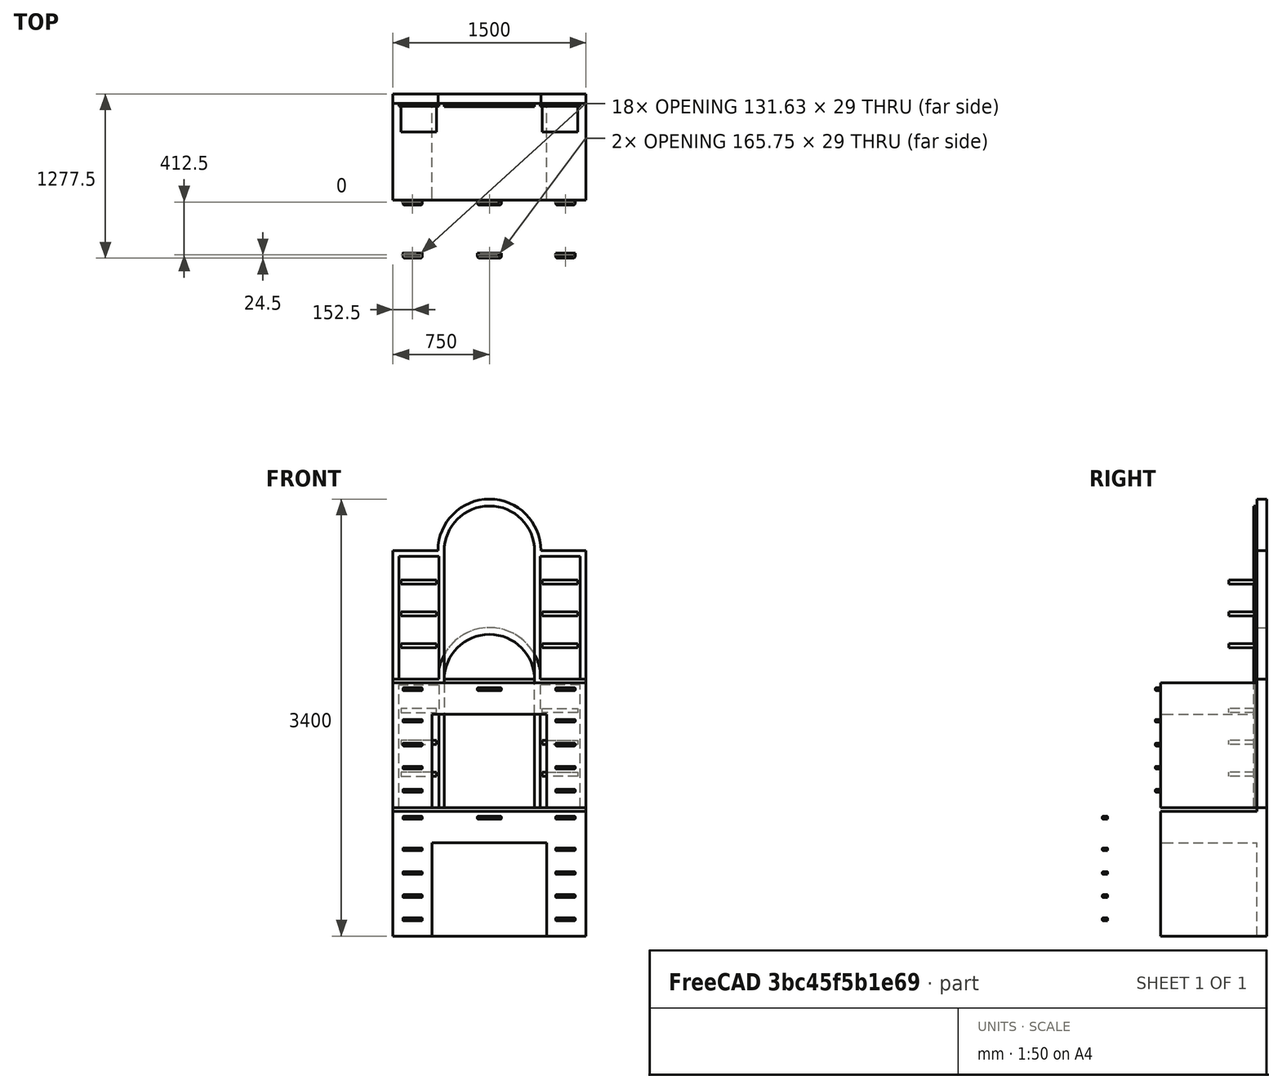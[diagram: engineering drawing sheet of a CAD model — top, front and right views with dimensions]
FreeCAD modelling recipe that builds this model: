
FCSTD DOCUMENT  (FreeCAD 1.0R39109 (Git))
Label: Dressing_Table
License: All rights reserved
LicenseURL: https://en.wikipedia.org/wiki/All_rights_reserved
objects: Sketcher::SketchObject×30, PartDesign::Fillet×22, PartDesign::Pad×18, PartDesign::Body×13, PartDesign::Pocket×12, PartDesign::ShapeBinder×12, PartDesign::Plane×12, Assembly::JointGroup×3, App::Link×3, Assembly::AssemblyObject×3, Part::FeaturePython×3, App::Part×2
note: 256 computed .brp shape members not serialized (recipe doc carries the construction recipe); baked Part::Feature solids carry a one-line shape summary decoded from their .brp

FEATURE [Sketcher::SketchObject] Sketch
  ArcFitTolerance = 1e-06
  AttachmentSupport = -> [XZ_Plane]
  FullyConstrained = true
  MakeInternals = false
  MapMode = 5
  Placement = pos=(0,0,0) rot=(1,0,0;1.5708rad)
  sketch-geometry (7):
    g0: LineSegment StartX=-750 StartY=-1000 StartZ=0 EndX=750 EndY=-1000 EndZ=0
    g1: LineSegment StartX=750 StartY=-1000 StartZ=0 EndX=750 EndY=1000 EndZ=0
    g2: LineSegment StartX=750 StartY=1000 StartZ=0 EndX=400 EndY=1000 EndZ=0
    g3: LineSegment StartX=-750 StartY=1000 StartZ=0 EndX=-750 EndY=-1000 EndZ=0
    g4: GeomPoint [constr] X=0 Y=0 Z=0
    g5: ArcOfCircle CenterX=1.35e-14 CenterY=1000 CenterZ=0 NormalX=0 NormalY=0 NormalZ=1 AngleXU=0 Radius=400 StartAngle=0 EndAngle=3.14159
    g6: LineSegment StartX=-400 StartY=1000 StartZ=0 EndX=-750 EndY=1000 EndZ=0
  constraints (18):
    c: Coincident(g0,g1)
    c: Coincident(g1,g2)
    c: Coincident(g6,g3)
    c: Coincident(g3,g0)
    c: Horizontal(g0)
    c: Horizontal(g2)
    c: Vertical(g1)
    c: Vertical(g3)
    c: Symmetric(g2,g0,g4)
    c: Coincident(g4,g-1)
    c: DistanceY(g1,g1) = 2000
    c: DistanceX(g6,g2) = 1500
    c: Symmetric(g1,g6,g5)
    c: Diameter(g5) = 800
    c: Coincident(g5,g6)
    c: Coincident(g5,g2)
    c: Horizontal(g6)
    c: Horizontal(g5,g2)
FEATURE [PartDesign::Pad] Pad
  Direction = (0,-1,2e-16)
  Length = 75
  Length2 = 10
  Placement = pos=(0,0,0) rot=(1,0,0;1.5708rad)
  Profile = -> Sketch
  ReferenceAxis = -> Sketch [N_Axis]
  Refine = true
  Suppressed = false
  Type = 0
FEATURE [Sketcher::SketchObject] Sketch001
  ArcFitTolerance = 1e-06
  AttachmentSupport = -> [Pad]
  FullyConstrained = false
  MakeInternals = false
  MapMode = 5
  Placement = pos=(0,-75,0) rot=(1,0,0;1.5708rad)
  sketch-geometry (14):
    g0: LineSegment [constr] StartX=0 StartY=0 StartZ=0 EndX=936.468 EndY=0 EndZ=0
    g1: LineSegment [constr] StartX=0 StartY=0 StartZ=0 EndX=-879.559 EndY=0 EndZ=0
    g2: ArcOfCircle CenterX=0 CenterY=995.137 CenterZ=0 NormalX=0 NormalY=0 NormalZ=1 AngleXU=0 Radius=351.618 StartAngle=0 EndAngle=3.14159
    g3: LineSegment StartX=-351.618 StartY=995.137 StartZ=0 EndX=-351.618 EndY=0 EndZ=0
    g4: LineSegment StartX=351.618 StartY=995.137 StartZ=0 EndX=351.618 EndY=0 EndZ=0
    g5: LineSegment StartX=-351.618 StartY=0 StartZ=0 EndX=351.618 EndY=0 EndZ=0
    g6: LineSegment StartX=393.332 StartY=955.725 StartZ=0 EndX=393.332 EndY=0 EndZ=0
    g7: LineSegment StartX=393.332 StartY=0 StartZ=0 EndX=704.851 EndY=0 EndZ=0
    g8: LineSegment StartX=704.851 StartY=0 StartZ=0 EndX=704.851 EndY=955.725 EndZ=0
    g9: LineSegment StartX=704.851 StartY=955.725 StartZ=0 EndX=393.332 EndY=955.725 EndZ=0
    g10: LineSegment StartX=-393.332 StartY=955.725 StartZ=0 EndX=-393.332 EndY=0 EndZ=0
    g11: LineSegment StartX=-393.332 StartY=0 StartZ=0 EndX=-704.851 EndY=0 EndZ=0
    g12: LineSegment StartX=-704.851 StartY=0 StartZ=0 EndX=-704.851 EndY=955.725 EndZ=0
    g13: LineSegment StartX=-704.851 StartY=955.725 StartZ=0 EndX=-393.332 EndY=955.725 EndZ=0
  constraints (30):
    c: Coincident(g0,g-1)
    c: Horizontal(g0)
    c: Coincident(g1,g0)
    c: PointOnObject(g1,g-1)
    c: PointOnObject(g2,g-2)
    c: PointOnObject(g3,g1)
    c: Vertical(g3)
    c: PointOnObject(g4,g0)
    c: Vertical(g4)
    c: Tangent(g4,g2) = 1.5708
    c: Tangent(g3,g2) = -1.5708
    c: Coincident(g5,g3)
    c: Coincident(g5,g4)
    c: Coincident(g6,g7)
    c: Coincident(g7,g8)
    c: Coincident(g8,g9)
    c: Coincident(g9,g6)
    c: Vertical(g6)
    c: Vertical(g8)
    c: Horizontal(g7)
    c: Horizontal(g9)
    c: PointOnObject(g7,g0)
    c: Coincident(g10,g11)
    c: Coincident(g11,g12)
    c: Coincident(g12,g13)
    c: Coincident(g13,g10)
    c: Vertical(g10)
    c: Vertical(g12)
    c: Horizontal(g11)
    c: Horizontal(g13)
FEATURE [PartDesign::Pad] Pad001
  BaseFeature = -> Pad
  Direction = (0,-1,2e-16)
  Length = 20
  Length2 = 10
  Placement = pos=(0,0,0) rot=(1,0,0;1.5708rad)
  Profile = -> Sketch001
  ReferenceAxis = -> Sketch001 [N_Axis]
  Refine = true
  Suppressed = false
  Type = 0
FEATURE [Sketcher::SketchObject] Sketch002
  ArcFitTolerance = 1e-06
  AttachmentSupport = -> [Pad001]
  ExternalGeometry = -> [Pad001]
  FullyConstrained = false
  MakeInternals = false
  MapMode = 5
  Placement = pos=(0,-95,2.09e-14) rot=(1,0,0;1.5708rad)
  sketch-geometry (27):
    g0: LineSegment StartX=-686.592 StartY=770.22 StartZ=0 EndX=-686.592 EndY=738.354 EndZ=0
    g1: LineSegment StartX=-686.592 StartY=738.354 StartZ=0 EndX=-411.592 EndY=738.354 EndZ=0
    g2: LineSegment StartX=-411.592 StartY=738.354 StartZ=0 EndX=-411.592 EndY=770.22 EndZ=0
    g3: LineSegment StartX=-411.592 StartY=770.22 StartZ=0 EndX=-686.592 EndY=770.22 EndZ=0
    g4: LineSegment StartX=-686.592 StartY=523.301 StartZ=0 EndX=-686.592 EndY=491.435 EndZ=0
    g5: LineSegment StartX=-686.592 StartY=491.435 StartZ=0 EndX=-411.592 EndY=491.435 EndZ=0
    g6: LineSegment StartX=-411.592 StartY=491.435 StartZ=0 EndX=-411.592 EndY=523.301 EndZ=0
    g7: LineSegment StartX=-411.592 StartY=523.301 StartZ=0 EndX=-686.592 EndY=523.301 EndZ=0
    g8: LineSegment StartX=-686.592 StartY=276.382 StartZ=0 EndX=-686.592 EndY=244.516 EndZ=0
    g9: LineSegment StartX=-686.592 StartY=244.516 StartZ=0 EndX=-411.592 EndY=244.516 EndZ=0
    g10: LineSegment StartX=-411.592 StartY=244.516 StartZ=0 EndX=-411.592 EndY=276.382 EndZ=0
    g11: LineSegment StartX=-411.592 StartY=276.382 StartZ=0 EndX=-686.592 EndY=276.382 EndZ=0
    g12: LineSegment [constr] StartX=-686.592 StartY=738.354 StartZ=0 EndX=-686.592 EndY=523.301 EndZ=0
    g13: LineSegment [constr] StartX=-686.592 StartY=491.435 StartZ=0 EndX=-686.592 EndY=276.382 EndZ=0
    g14: LineSegment [constr] StartX=-549.092 StartY=477.863 StartZ=0 EndX=-549.092 EndY=955.725 EndZ=0
    g15: LineSegment StartX=686.592 StartY=738.354 StartZ=0 EndX=411.592 EndY=738.354 EndZ=0
    g16: LineSegment StartX=411.592 StartY=770.22 StartZ=0 EndX=686.592 EndY=770.22 EndZ=0
    g17: LineSegment StartX=411.592 StartY=738.354 StartZ=0 EndX=411.592 EndY=770.22 EndZ=0
    g18: LineSegment StartX=686.592 StartY=770.22 StartZ=0 EndX=686.592 EndY=738.354 EndZ=0
    g19: LineSegment StartX=411.592 StartY=523.301 StartZ=0 EndX=686.592 EndY=523.301 EndZ=0
    g20: LineSegment StartX=411.592 StartY=491.435 StartZ=0 EndX=411.592 EndY=523.301 EndZ=0
    g21: LineSegment StartX=686.592 StartY=491.435 StartZ=0 EndX=411.592 EndY=491.435 EndZ=0
    g22: LineSegment StartX=686.592 StartY=523.301 StartZ=0 EndX=686.592 EndY=491.435 EndZ=0
    g23: LineSegment StartX=411.592 StartY=244.516 StartZ=0 EndX=411.592 EndY=276.382 EndZ=0
    g24: LineSegment StartX=686.592 StartY=244.516 StartZ=0 EndX=411.592 EndY=244.516 EndZ=0
    g25: LineSegment StartX=411.592 StartY=276.382 StartZ=0 EndX=686.592 EndY=276.382 EndZ=0
    g26: LineSegment StartX=686.592 StartY=276.382 StartZ=0 EndX=686.592 EndY=244.516 EndZ=0
  constraints (66):
    c: Coincident(g0,g1)
    c: Coincident(g1,g2)
    c: Coincident(g2,g3)
    c: Coincident(g3,g0)
    c: Vertical(g0)
    c: Vertical(g2)
    c: Horizontal(g1)
    c: Horizontal(g3)
    c: Coincident(g4,g5)
    c: Coincident(g5,g6)
    c: Coincident(g6,g7)
    c: Coincident(g7,g4)
    c: Vertical(g4)
    c: Vertical(g6)
    c: Horizontal(g5)
    c: Horizontal(g7)
    c: Coincident(g8,g9)
    c: Coincident(g9,g10)
    c: Coincident(g10,g11)
    c: Coincident(g11,g8)
    c: Vertical(g8)
    c: Vertical(g10)
    c: Horizontal(g9)
    c: Horizontal(g11)
    c: Coincident(g12,g0)
    c: Coincident(g12,g4)
    c: Vertical(g12)
    c: Coincident(g13,g4)
    c: Coincident(g13,g8)
    c: Vertical(g13)
    c: Equal(g12,g13)
    c: Equal(g2,g6)
    c: Equal(g6,g10)
    c: Equal(g11,g7)
    c: Equal(g7,g3)
    c: DistanceX(g3,g3) = 275
    c: Symmetric(g2,g0,g14)
    c: Symmetric(g-5,g-5,g14)
    c: Coincident(g18,g15)
    c: Coincident(g15,g17)
    c: Coincident(g17,g16)
    c: Coincident(g16,g18)
    c: Vertical(g18)
    c: Vertical(g17)
    c: Horizontal(g15)
    c: Horizontal(g16)
    c: Coincident(g22,g21)
    c: Coincident(g21,g20)
    c: Coincident(g20,g19)
    c: Coincident(g19,g22)
    c: Vertical(g22)
    c: Vertical(g20)
    c: Horizontal(g21)
    c: Horizontal(g19)
    c: Coincident(g26,g24)
    c: Coincident(g24,g23)
    c: Coincident(g23,g25)
    c: Coincident(g25,g26)
    c: Vertical(g26)
    c: Vertical(g23)
    c: Horizontal(g24)
    c: Horizontal(g25)
    c: Equal(g17,g20)
    c: Equal(g20,g23)
    c: Equal(g25,g19)
    c: Equal(g19,g16)
FEATURE [PartDesign::Pad] Pad002
  BaseFeature = -> Pad001
  Direction = (0,-1,2e-16)
  Length = 200
  Length2 = 10
  Placement = pos=(0,0,0) rot=(1,0,0;1.5708rad)
  Profile = -> Sketch002
  ReferenceAxis = -> Sketch002 [N_Axis]
  Refine = true
  Suppressed = false
  Type = 0
FEATURE [Sketcher::SketchObject] Sketch003
  ArcFitTolerance = 1e-06
  AttachmentSupport = -> [Pad002]
  ExternalGeometry = -> [Pad002]
  FullyConstrained = true
  MakeInternals = false
  MapMode = 5
  Placement = pos=(0,-75,0) rot=(1,0,0;1.5708rad)
  sketch-geometry (4):
    g0: LineSegment StartX=-750 StartY=-1000 StartZ=0 EndX=750 EndY=-1000 EndZ=0
    g1: LineSegment StartX=750 StartY=-1000 StartZ=0 EndX=750 EndY=-30 EndZ=0
    g2: LineSegment StartX=750 StartY=-30 StartZ=0 EndX=-750 EndY=-30 EndZ=0
    g3: LineSegment StartX=-750 StartY=-30 StartZ=0 EndX=-750 EndY=-1000 EndZ=0
  constraints (11):
    c: Coincident(g0,g1)
    c: Coincident(g1,g2)
    c: Coincident(g2,g3)
    c: Coincident(g3,g0)
    c: Horizontal(g0)
    c: Horizontal(g2)
    c: Vertical(g1)
    c: Vertical(g3)
    c: Coincident(g0,g-3)
    c: PointOnObject(g1,g-4)
    c: DistanceY(g1,g1) = 970
FEATURE [PartDesign::Pad] Pad003
  BaseFeature = -> Pad002
  Direction = (0,-1,2e-16)
  Length = 750
  Length2 = 10
  Placement = pos=(0,0,0) rot=(1,0,0;1.5708rad)
  Profile = -> Sketch003
  ReferenceAxis = -> Sketch003 [N_Axis]
  Suppressed = false
  Type = 0
FEATURE [Sketcher::SketchObject] Sketch004
  ArcFitTolerance = 1e-06
  AttachmentSupport = -> [Pad003]
  ExternalGeometry = -> [Pad003]
  FullyConstrained = true
  MakeInternals = false
  MapMode = 5
  Placement = pos=(0,-825,1.897e-13) rot=(1,0,0;1.5708rad)
  sketch-geometry (4):
    g0: LineSegment StartX=-445 StartY=-1000 StartZ=0 EndX=445 EndY=-1000 EndZ=0
    g1: LineSegment StartX=445 StartY=-1000 StartZ=0 EndX=445 EndY=-275 EndZ=0
    g2: LineSegment StartX=445 StartY=-275 StartZ=0 EndX=-445 EndY=-275 EndZ=0
    g3: LineSegment StartX=-445 StartY=-275 StartZ=0 EndX=-445 EndY=-1000 EndZ=0
  constraints (11):
    c: Coincident(g0,g1)
    c: Coincident(g1,g2)
    c: Coincident(g2,g3)
    c: Coincident(g3,g0)
    c: Horizontal(g0)
    c: Vertical(g1)
    c: Vertical(g3)
    c: PointOnObject(g0,g-3)
    c: DistanceX(g2,g2) = 890
    c: DistanceY(g1,g1) = 725
    c: Symmetric(g1,g2,g-2)
FEATURE [PartDesign::Pocket] Pocket
  BaseFeature = -> Pad003
  Direction = (0,1,-2e-16)
  Length = 750
  Length2 = 5
  Placement = pos=(0,0,0) rot=(1,0,0;1.5708rad)
  Profile = -> Sketch004
  ReferenceAxis = -> Sketch004 [N_Axis]
  Suppressed = false
  Type = 0
FEATURE [Sketcher::SketchObject] Sketch005
  ArcFitTolerance = 1e-06
  AttachmentSupport = -> [Pocket]
  ExternalGeometry = -> [Pocket]
  FullyConstrained = true
  MakeInternals = false
  MapMode = 5
  Placement = pos=(0,-825,1.897e-13) rot=(1,0,0;1.5708rad)
  sketch-geometry (24):
    g0: LineSegment StartX=-445 StartY=-275 StartZ=0 EndX=-445 EndY=-30 EndZ=0
    g1: LineSegment StartX=-445 StartY=-30 StartZ=0 EndX=-750 EndY=-30 EndZ=0
    g2: LineSegment StartX=-750 StartY=-30 StartZ=0 EndX=-750 EndY=-275 EndZ=0
    g3: LineSegment StartX=-750 StartY=-275 StartZ=0 EndX=-445 EndY=-275 EndZ=0
    g4: LineSegment StartX=-445 StartY=-460 StartZ=0 EndX=-750 EndY=-460 EndZ=0
    g5: LineSegment StartX=-750 StartY=-460 StartZ=0 EndX=-750 EndY=-640 EndZ=0
    g6: LineSegment StartX=-750 StartY=-640 StartZ=0 EndX=-445 EndY=-640 EndZ=0
    g7: LineSegment StartX=-445 StartY=-640 StartZ=0 EndX=-445 EndY=-460 EndZ=0
    g8: LineSegment StartX=-750 StartY=-820 StartZ=0 EndX=-445 EndY=-820 EndZ=0
    g9: LineSegment StartX=-750 StartY=-820 StartZ=0 EndX=-750 EndY=-1000 EndZ=0
    g10: LineSegment StartX=-750 StartY=-1000 StartZ=0 EndX=-445 EndY=-1000 EndZ=0
    g11: LineSegment StartX=-445 StartY=-1000 StartZ=0 EndX=-445 EndY=-820 EndZ=0
    g12: LineSegment StartX=750 StartY=-30 StartZ=0 EndX=750 EndY=-275 EndZ=0
    g13: LineSegment StartX=445 StartY=-30 StartZ=0 EndX=750 EndY=-30 EndZ=0
    g14: LineSegment StartX=750 StartY=-275 StartZ=0 EndX=445 EndY=-275 EndZ=0
    g15: LineSegment StartX=445 StartY=-460 StartZ=0 EndX=750 EndY=-460 EndZ=0
    g16: LineSegment StartX=750 StartY=-460 StartZ=0 EndX=750 EndY=-640 EndZ=0
    g17: LineSegment StartX=750 StartY=-640 StartZ=0 EndX=445 EndY=-640 EndZ=0
    g18: LineSegment StartX=445 StartY=-640 StartZ=0 EndX=445 EndY=-460 EndZ=0
    g19: LineSegment StartX=445 StartY=-1000 StartZ=0 EndX=445 EndY=-820 EndZ=0
    g20: LineSegment StartX=750 StartY=-1000 StartZ=0 EndX=445 EndY=-1000 EndZ=0
    g21: LineSegment StartX=750 StartY=-820 StartZ=0 EndX=750 EndY=-1000 EndZ=0
    g22: LineSegment StartX=750 StartY=-820 StartZ=0 EndX=445 EndY=-820 EndZ=0
    g23: LineSegment StartX=445 StartY=-30 StartZ=0 EndX=445 EndY=-275 EndZ=0
  constraints (67):
    c: Coincident(g0,g1)
    c: Vertical(g0)
    c: Horizontal(g1)
    c: Coincident(g0,g-6)
    c: Coincident(g1,g2)
    c: PointOnObject(g2,g-5)
    c: Coincident(g2,g3)
    c: Coincident(g3,g0)
    c: Horizontal(g3)
    c: PointOnObject(g4,g-6)
    c: PointOnObject(g4,g-5)
    c: Horizontal(g4)
    c: Coincident(g4,g5)
    c: PointOnObject(g5,g-5)
    c: Coincident(g5,g6)
    c: PointOnObject(g6,g-6)
    c: Horizontal(g6)
    c: Coincident(g6,g7)
    c: PointOnObject(g8,g-5)
    c: PointOnObject(g8,g-6)
    c: Horizontal(g8)
    c: Coincident(g9,g10)
    c: PointOnObject(g10,g-6)
    c: Horizontal(g10)
    c: Coincident(g10,g11)
    c: Coincident(g11,g8)
    c: Coincident(g9,g-5)
    c: DistanceY(g9,g9) = 180
    c: Coincident(g1,g-5)
    c: Horizontal(g13)
    c: Coincident(g13,g12)
    c: Coincident(g12,g14)
    c: Horizontal(g14)
    c: Horizontal(g15)
    c: Coincident(g15,g16)
    c: Coincident(g16,g17)
    c: Horizontal(g17)
    c: Coincident(g17,g18)
    c: Horizontal(g22)
    c: Coincident(g21,g20)
    c: Horizontal(g20)
    c: Coincident(g20,g19)
    c: Coincident(g19,g22)
    c: Coincident(g12,g-4)
    c: Equal(g14,g13)
    c: Horizontal(g15,g4)
    c: Horizontal(g17,g6)
    c: Horizontal(g22,g8)
    c: Horizontal(g19,g10)
    c: Vertical(g15,g17)
    c: Vertical(g17,g22)
    c: Vertical(g22,g19)
    c: Vertical(g19,g14)
    c: Vertical(g21,g20)
    c: Vertical(g20,g12)
    c: Coincident(g23,g13)
    c: Coincident(g23,g14)
    c: Vertical(g23)
    c: Coincident(g14,g-3)
    c: Coincident(g7,g4)
    c: Equal(g5,g9)
    c: Coincident(g18,g15)
    c: Vertical(g15,g12)
    c: Coincident(g22,g21)
    c: Coincident(g9,g8)
    c: DistanceY(g8,g5) = 180
    c: Vertical(g16,g21)
FEATURE [PartDesign::Pad] Pad004
  BaseFeature = -> Pocket
  Direction = (0,-1,2e-16)
  Length = 25
  Length2 = 10
  Placement = pos=(0,0,0) rot=(1,0,0;1.5708rad)
  Profile = -> Sketch005
  ReferenceAxis = -> Sketch005 [N_Axis]
  Reversed = true
  Suppressed = false
  Type = 0
FEATURE [Sketcher::SketchObject] Sketch006
  ArcFitTolerance = 1e-06
  AttachmentSupport = -> [Pad004]
  ExternalGeometry = -> [Pad004]
  FullyConstrained = true
  MakeInternals = false
  MapMode = 5
  Placement = pos=(0,-825,1.897e-13) rot=(1,0,0;1.5708rad)
  sketch-geometry (20):
    g0: LineSegment StartX=-750 StartY=-275 StartZ=0 EndX=-750 EndY=-460 EndZ=0
    g1: LineSegment StartX=-750 StartY=-460 StartZ=0 EndX=-445 EndY=-460 EndZ=0
    g2: LineSegment StartX=-445 StartY=-460 StartZ=0 EndX=-445 EndY=-275 EndZ=0
    g3: LineSegment StartX=-445 StartY=-275 StartZ=0 EndX=-750 EndY=-275 EndZ=0
    g4: LineSegment StartX=-750 StartY=-640 StartZ=0 EndX=-750 EndY=-820 EndZ=0
    g5: LineSegment StartX=-750 StartY=-820 StartZ=0 EndX=-445 EndY=-820 EndZ=0
    g6: LineSegment StartX=-445 StartY=-820 StartZ=0 EndX=-445 EndY=-640 EndZ=0
    g7: LineSegment StartX=-445 StartY=-640 StartZ=0 EndX=-750 EndY=-640 EndZ=0
    g8: LineSegment StartX=445 StartY=-275 StartZ=0 EndX=445 EndY=-460 EndZ=0
    g9: LineSegment StartX=445 StartY=-460 StartZ=0 EndX=750 EndY=-460 EndZ=0
    g10: LineSegment StartX=750 StartY=-460 StartZ=0 EndX=750 EndY=-275 EndZ=0
    g11: LineSegment StartX=750 StartY=-275 StartZ=0 EndX=445 EndY=-275 EndZ=0
    g12: LineSegment StartX=445 StartY=-640 StartZ=0 EndX=445 EndY=-820 EndZ=0
    g13: LineSegment StartX=445 StartY=-820 StartZ=0 EndX=750 EndY=-820 EndZ=0
    g14: LineSegment StartX=750 StartY=-820 StartZ=0 EndX=750 EndY=-640 EndZ=0
    g15: LineSegment StartX=750 StartY=-640 StartZ=0 EndX=445 EndY=-640 EndZ=0
    g16: LineSegment StartX=-445 StartY=-30 StartZ=0 EndX=-445 EndY=-275 EndZ=0
    g17: LineSegment StartX=-445 StartY=-275 StartZ=0 EndX=445 EndY=-275 EndZ=0
    g18: LineSegment StartX=445 StartY=-275 StartZ=0 EndX=445 EndY=-30 EndZ=0
    g19: LineSegment StartX=445 StartY=-30 StartZ=0 EndX=-445 EndY=-30 EndZ=0
  constraints (50):
    c: Coincident(g0,g1)
    c: Coincident(g1,g2)
    c: Coincident(g2,g3)
    c: Coincident(g3,g0)
    c: Vertical(g0)
    c: Vertical(g2)
    c: Horizontal(g1)
    c: Horizontal(g3)
    c: Coincident(g0,g-4)
    c: Coincident(g1,g-3)
    c: Coincident(g4,g5)
    c: Coincident(g5,g6)
    c: Coincident(g6,g7)
    c: Coincident(g7,g4)
    c: Vertical(g4)
    c: Vertical(g6)
    c: Horizontal(g5)
    c: Horizontal(g7)
    c: Coincident(g4,g-6)
    c: Coincident(g5,g-5)
    c: Coincident(g8,g9)
    c: Coincident(g9,g10)
    c: Coincident(g10,g11)
    c: Coincident(g11,g8)
    c: Vertical(g8)
    c: Vertical(g10)
    c: Horizontal(g9)
    c: Horizontal(g11)
    c: Coincident(g8,g-8)
    c: Coincident(g9,g-9)
    c: Coincident(g12,g13)
    c: Coincident(g13,g14)
    c: Coincident(g14,g15)
    c: Coincident(g15,g12)
    c: Vertical(g12)
    c: Vertical(g14)
    c: Horizontal(g13)
    c: Horizontal(g15)
    c: Coincident(g12,g-10)
    c: Coincident(g13,g-11)
    c: Coincident(g16,g17)
    c: Coincident(g17,g18)
    c: Coincident(g18,g19)
    c: Coincident(g19,g16)
    c: Vertical(g16)
    c: Vertical(g18)
    c: Horizontal(g17)
    c: Horizontal(g19)
    c: Coincident(g16,g-7)
    c: Coincident(g17,g8)
FEATURE [PartDesign::Pad] Pad005
  BaseFeature = -> Pad004
  Direction = (0,-1,2e-16)
  Length = 25
  Length2 = 10
  Placement = pos=(0,0,0) rot=(1,0,0;1.5708rad)
  Profile = -> Sketch006
  ReferenceAxis = -> Sketch006 [N_Axis]
  Reversed = true
  Suppressed = false
  Type = 0
FEATURE [PartDesign::Body] Body
  AllowCompound = false
  Group = -> [Sketch,Pad,Sketch001,Pad001,Sketch002,Pad002,Sketch003,Pad003,Sketch004,Pocket,Sketch005,Pad004,Sketch006,Pad005]
  Origin = -> Origin
  Placement = pos=(0,412.5,0) rot=(0,0,1;0rad)
  Tip = -> Pad005
FEATURE [Assembly::JointGroup] Joints
FEATURE [App::Link] dressing_table001  label="dressing_table002"
  LinkPlacement = pos=(0,412.5,1000) rot=(0,0,1;0rad)
  LinkedObject = -> Body
  Placement = pos=(0,412.5,1000) rot=(0,0,1;0rad)
FEATURE [Assembly::AssemblyObject] Assembly  label="body_a"
  Group = -> [Joints,dressing_table001]
  Origin = -> Origin003
  Placement = pos=(0,412.5,1000) rot=(0,0,1;0rad)
  Type = Assembly
FEATURE [PartDesign::ShapeBinder] CopyPocket001
  Placement = pos=(0,0,0) rot=(1,0,0;1.5708rad)
  TraceSupport = false
FEATURE [PartDesign::Plane] DatumPlane
  AttachmentSupport = -> [CopyPocket001]
  Length = 214.996
  MapMode = 5
  Placement = pos=(0,-825,6.6e-15) rot=(1,0,0;1.5708rad)
  ResizeMode = 0
  Width = 144.392
FEATURE [Sketcher::SketchObject] Sketch008
  ArcFitTolerance = 1e-06
  AttachmentSupport = -> [CopyPocket001]
  ExternalGeometry = -> [CopyPocket001]
  FullyConstrained = true
  MakeInternals = false
  MapMode = 5
  Placement = pos=(0,-825,1.897e-13) rot=(1,0,0;1.5708rad)
  sketch-geometry (4):
    g0: LineSegment StartX=-92.8734 StartY=-68.8715 StartZ=0 EndX=-92.8734 EndY=-90.1429 EndZ=0
    g1: LineSegment StartX=-92.8734 StartY=-90.1429 StartZ=0 EndX=92.8734 EndY=-90.1429 EndZ=0
    g2: LineSegment StartX=92.8734 StartY=-90.1429 StartZ=0 EndX=92.8734 EndY=-68.8715 EndZ=0
    g3: LineSegment StartX=92.8734 StartY=-68.8715 StartZ=0 EndX=-92.8734 EndY=-68.8715 EndZ=0
  constraints (10):
    c: Coincident(g0,g1)
    c: Coincident(g1,g2)
    c: Coincident(g2,g3)
    c: Coincident(g3,g0)
    c: Vertical(g0)
    c: Vertical(g2)
    c: Horizontal(g1)
    c: Horizontal(g3)
    c: Coincident(g0,g-3)
    c: Coincident(g1,g-5)
FEATURE [PartDesign::Pad] Pad006
  Direction = (0,-1,2e-16)
  Length = 40
  Length2 = 10
  Placement = pos=(0,0,0) rot=(1,0,0;1.5708rad)
  Profile = -> Sketch008
  ReferenceAxis = -> Sketch008 [N_Axis]
  Refine = true
  Suppressed = false
  Type = 0
FEATURE [Sketcher::SketchObject] Sketch009
  ArcFitTolerance = 1e-06
  AttachmentSupport = -> [Pad006]
  ExternalGeometry = -> [Pad006]
  FullyConstrained = true
  MakeInternals = false
  MapMode = 5
  Placement = pos=(0,-7.6e-15,-68.8715) rot=(0,0,1;3.14159rad)
  sketch-geometry (4):
    g0: LineSegment StartX=-77.8734 StartY=850 StartZ=0 EndX=-77.8734 EndY=826 EndZ=0
    g1: LineSegment StartX=77.8734 StartY=850 StartZ=0 EndX=77.8734 EndY=826 EndZ=0
    g2: LineSegment StartX=-77.8734 StartY=850 StartZ=0 EndX=77.8734 EndY=850 EndZ=0
    g3: LineSegment StartX=-77.8734 StartY=826 StartZ=0 EndX=77.8734 EndY=826 EndZ=0
  constraints (12):
    c: Coincident(g2,g0)
    c: Coincident(g2,g1)
    c: Horizontal(g2)
    c: DistanceX(g-3,g0) = 15
    c: DistanceX(g1,g-3) = 15
    c: Vertical(g0)
    c: Vertical(g1)
    c: DistanceY(g0,g-4) = 15
    c: DistanceY(g-3,g0) = 1
    c: DistanceY(g-3,g1) = 1
    c: Coincident(g3,g0)
    c: Coincident(g3,g1)
FEATURE [PartDesign::Pocket] Pocket002
  BaseFeature = -> Pad006
  Direction = (0,0,-1)
  Length = 5
  Length2 = 5
  Placement = pos=(0,0,0) rot=(1,0,0;1.5708rad)
  Profile = -> Sketch009
  ReferenceAxis = -> Sketch009 [N_Axis]
  Refine = true
  Suppressed = false
  Type = 1
FEATURE [PartDesign::Fillet] Fillet
  Base = -> Pocket002 [Edge22,Edge21,Edge4,Edge20]
  BaseFeature = -> Pocket002
  Placement = pos=(0,0,0) rot=(1,0,0;1.5708rad)
  Radius = 15
  Refine = true
  SupportTransform = false
  Suppressed = false
  UseAllEdges = false
FEATURE [PartDesign::Fillet] Fillet001
  Base = -> Fillet [Edge8,Edge20,Edge10,Edge26]
  BaseFeature = -> Fillet
  Placement = pos=(0,0,0) rot=(1,0,0;1.5708rad)
  Radius = 5
  Refine = true
  SupportTransform = false
  Suppressed = false
  UseAllEdges = false
FEATURE [PartDesign::Body] Body001
  AllowCompound = false
  Group = -> [DatumPlane,CopyPocket001,Sketch008,Pad006,Sketch009,Pocket002,Fillet,Fillet001]
  Origin = -> Origin005
  Tip = -> Fillet001
FEATURE [PartDesign::ShapeBinder] CopyPocket002
  Placement = pos=(0,0,0) rot=(1,0,0;1.5708rad)
  TraceSupport = false
FEATURE [PartDesign::Plane] DatumPlane001
  AttachmentSupport = -> [CopyPocket002]
  Length = 755.028
  MapMode = 5
  Placement = pos=(0,-825,6.6e-15) rot=(1,0,0;1.5708rad)
  ResizeMode = 0
  Width = 171.855
FEATURE [Sketcher::SketchObject] Sketch010
  ArcFitTolerance = 1e-06
  AttachmentSupport = -> [CopyPocket002]
  ExternalGeometry = -> [CopyPocket002]
  FullyConstrained = true
  MakeInternals = false
  MapMode = 5
  Placement = pos=(0,-825,1.897e-13) rot=(1,0,0;1.5708rad)
  sketch-geometry (4):
    g0: LineSegment StartX=-673.316 StartY=-90.1429 StartZ=0 EndX=-521.684 EndY=-90.1429 EndZ=0
    g1: LineSegment StartX=-521.684 StartY=-90.1429 StartZ=0 EndX=-521.684 EndY=-68.8715 EndZ=0
    g2: LineSegment StartX=-521.684 StartY=-68.8715 StartZ=0 EndX=-673.316 EndY=-68.8715 EndZ=0
    g3: LineSegment StartX=-673.316 StartY=-68.8715 StartZ=0 EndX=-673.316 EndY=-90.1429 EndZ=0
  constraints (10):
    c: Coincident(g0,g1)
    c: Coincident(g1,g2)
    c: Coincident(g2,g3)
    c: Coincident(g3,g0)
    c: Horizontal(g0)
    c: Horizontal(g2)
    c: Vertical(g1)
    c: Vertical(g3)
    c: Coincident(g0,g-4)
    c: Coincident(g1,g-3)
FEATURE [PartDesign::Pad] Pad007
  Direction = (0,-1,2e-16)
  Length = 40
  Length2 = 10
  Placement = pos=(0,0,0) rot=(1,0,0;1.5708rad)
  Profile = -> Sketch010
  ReferenceAxis = -> Sketch010 [N_Axis]
  Refine = true
  Suppressed = false
  Type = 0
FEATURE [Sketcher::SketchObject] Sketch011
  ArcFitTolerance = 1e-06
  AttachmentSupport = -> [Pad007]
  ExternalGeometry = -> [Pad007]
  FullyConstrained = true
  MakeInternals = false
  MapMode = 5
  Placement = pos=(0,-7.6e-15,-68.8715) rot=(0,0,1;3.14159rad)
  sketch-geometry (4):
    g0: LineSegment StartX=536.684 StartY=850 StartZ=0 EndX=536.684 EndY=826 EndZ=0
    g1: LineSegment StartX=536.684 StartY=826 StartZ=0 EndX=658.316 EndY=826 EndZ=0
    g2: LineSegment StartX=658.316 StartY=826 StartZ=0 EndX=658.316 EndY=850 EndZ=0
    g3: LineSegment StartX=658.316 StartY=850 StartZ=0 EndX=536.684 EndY=850 EndZ=0
  constraints (12):
    c: Coincident(g0,g1)
    c: Coincident(g1,g2)
    c: Coincident(g2,g3)
    c: Coincident(g3,g0)
    c: Vertical(g0)
    c: Vertical(g2)
    c: Horizontal(g1)
    c: Horizontal(g3)
    c: DistanceY(g-4,g1) = 1
    c: DistanceX(g1,g-4) = 15
    c: DistanceY(g2,g-4) = 15
    c: DistanceX(g-3,g0) = 15
FEATURE [PartDesign::Pocket] Pocket003
  BaseFeature = -> Pad007
  Direction = (0,0,-1)
  Length = 5
  Length2 = 5
  Placement = pos=(0,0,0) rot=(1,0,0;1.5708rad)
  Profile = -> Sketch011
  ReferenceAxis = -> Sketch011 [N_Axis]
  Refine = true
  Suppressed = false
  Type = 1
FEATURE [PartDesign::Fillet] Fillet002
  Base = -> Pocket003 [Edge19,Edge14,Edge23,Edge11]
  BaseFeature = -> Pocket003
  Placement = pos=(0,0,0) rot=(1,0,0;1.5708rad)
  Radius = 15
  Refine = true
  SupportTransform = false
  Suppressed = false
  UseAllEdges = false
FEATURE [PartDesign::Fillet] Fillet003
  Base = -> Fillet002 [Edge21,Edge4,Edge32,Edge10]
  BaseFeature = -> Fillet002
  Placement = pos=(0,0,0) rot=(1,0,0;1.5708rad)
  Radius = 5
  Refine = true
  SupportTransform = false
  Suppressed = false
  UseAllEdges = false
FEATURE [PartDesign::Body] Body002
  AllowCompound = false
  Group = -> [DatumPlane001,CopyPocket002,Sketch010,Pad007,Sketch011,Pocket003,Fillet002,Fillet003]
  Origin = -> Origin007
  Tip = -> Fillet003
FEATURE [PartDesign::ShapeBinder] CopyPocket003
  Placement = pos=(0,0,0) rot=(1,0,0;1.5708rad)
  TraceSupport = false
FEATURE [PartDesign::Plane] DatumPlane002
  AttachmentSupport = -> [CopyPocket003]
  Length = 798.615
  MapMode = 5
  Placement = pos=(0,-825,6.6e-15) rot=(1,0,0;1.5708rad)
  ResizeMode = 0
  Width = 460.441
FEATURE [Sketcher::SketchObject] Sketch012
  ArcFitTolerance = 1e-06
  AttachmentSupport = -> [CopyPocket003]
  ExternalGeometry = -> [CopyPocket003]
  FullyConstrained = true
  MakeInternals = false
  MapMode = 5
  Placement = pos=(0,-825,1.897e-13) rot=(1,0,0;1.5708rad)
  sketch-geometry (4):
    g0: LineSegment StartX=-673.316 StartY=-313.872 StartZ=0 EndX=-673.316 EndY=-335.143 EndZ=0
    g1: LineSegment StartX=-673.316 StartY=-335.143 StartZ=0 EndX=-521.684 EndY=-335.143 EndZ=0
    g2: LineSegment StartX=-521.684 StartY=-335.143 StartZ=0 EndX=-521.684 EndY=-313.872 EndZ=0
    g3: LineSegment StartX=-521.684 StartY=-313.872 StartZ=0 EndX=-673.316 EndY=-313.872 EndZ=0
  constraints (10):
    c: Coincident(g0,g1)
    c: Coincident(g1,g2)
    c: Coincident(g2,g3)
    c: Coincident(g3,g0)
    c: Vertical(g0)
    c: Vertical(g2)
    c: Horizontal(g1)
    c: Horizontal(g3)
    c: Coincident(g0,g-4)
    c: Coincident(g1,g-3)
FEATURE [PartDesign::Pad] Pad008
  Direction = (0,-1,2e-16)
  Length = 40
  Length2 = 10
  Placement = pos=(0,0,0) rot=(1,0,0;1.5708rad)
  Profile = -> Sketch012
  ReferenceAxis = -> Sketch012 [N_Axis]
  Refine = true
  Suppressed = false
  Type = 0
FEATURE [Sketcher::SketchObject] Sketch013
  ArcFitTolerance = 1e-06
  AttachmentSupport = -> [Pad008]
  ExternalGeometry = -> [Pad008]
  FullyConstrained = true
  MakeInternals = false
  MapMode = 5
  Placement = pos=(0,-3.45e-14,-313.872) rot=(0,0,1;3.14159rad)
  sketch-geometry (4):
    g0: LineSegment StartX=536.684 StartY=850 StartZ=0 EndX=536.684 EndY=826 EndZ=0
    g1: LineSegment StartX=536.684 StartY=826 StartZ=0 EndX=658.316 EndY=826 EndZ=0
    g2: LineSegment StartX=658.316 StartY=826 StartZ=0 EndX=658.316 EndY=850 EndZ=0
    g3: LineSegment StartX=658.316 StartY=850 StartZ=0 EndX=536.684 EndY=850 EndZ=0
  constraints (12):
    c: Coincident(g0,g1)
    c: Coincident(g1,g2)
    c: Coincident(g2,g3)
    c: Coincident(g3,g0)
    c: Vertical(g0)
    c: Vertical(g2)
    c: Horizontal(g1)
    c: Horizontal(g3)
    c: DistanceY(g-4,g1) = 1
    c: DistanceX(g1,g-4) = 15
    c: DistanceY(g0,g-3) = 15
    c: DistanceX(g-3,g0) = 15
FEATURE [PartDesign::Pocket] Pocket004
  BaseFeature = -> Pad008
  Direction = (0,0,-1)
  Length = 5
  Length2 = 5
  Placement = pos=(0,0,0) rot=(1,0,0;1.5708rad)
  Profile = -> Sketch013
  ReferenceAxis = -> Sketch013 [N_Axis]
  Refine = true
  Suppressed = false
  Type = 1
FEATURE [PartDesign::Fillet] Fillet004
  Base = -> Pocket004 [Edge20,Edge4,Edge21,Edge22]
  BaseFeature = -> Pocket004
  Placement = pos=(0,0,0) rot=(1,0,0;1.5708rad)
  Radius = 15
  Refine = true
  SupportTransform = false
  Suppressed = false
  UseAllEdges = false
FEATURE [PartDesign::Fillet] Fillet005
  Base = -> Fillet004 [Edge8,Edge20,Edge10,Edge26]
  BaseFeature = -> Fillet004
  Placement = pos=(0,0,0) rot=(1,0,0;1.5708rad)
  Radius = 5
  Refine = true
  SupportTransform = false
  Suppressed = false
  UseAllEdges = false
FEATURE [PartDesign::Body] Body003
  AllowCompound = false
  Group = -> [DatumPlane002,CopyPocket003,Sketch012,Pad008,Sketch013,Pocket004,Fillet004,Fillet005]
  Origin = -> Origin008
  Tip = -> Fillet005
FEATURE [PartDesign::ShapeBinder] CopyPocket004
  Placement = pos=(0,0,0) rot=(1,0,0;1.5708rad)
  TraceSupport = false
FEATURE [PartDesign::Plane] DatumPlane003
  AttachmentSupport = -> [CopyPocket004]
  Length = 821.715
  MapMode = 5
  Placement = pos=(0,-825,6.6e-15) rot=(1,0,0;1.5708rad)
  ResizeMode = 0
  Width = 668.542
FEATURE [Sketcher::SketchObject] Sketch014
  ArcFitTolerance = 1e-06
  AttachmentSupport = -> [CopyPocket004]
  ExternalGeometry = -> [CopyPocket004]
  FullyConstrained = true
  MakeInternals = false
  MapMode = 5
  Placement = pos=(0,-825,1.897e-13) rot=(1,0,0;1.5708rad)
  sketch-geometry (4):
    g0: LineSegment StartX=-673.316 StartY=-498.872 StartZ=0 EndX=-673.316 EndY=-520.143 EndZ=0
    g1: LineSegment StartX=-673.316 StartY=-520.143 StartZ=0 EndX=-521.684 EndY=-520.143 EndZ=0
    g2: LineSegment StartX=-521.684 StartY=-520.143 StartZ=0 EndX=-521.684 EndY=-498.872 EndZ=0
    g3: LineSegment StartX=-521.684 StartY=-498.872 StartZ=0 EndX=-673.316 EndY=-498.872 EndZ=0
  constraints (10):
    c: Coincident(g0,g1)
    c: Coincident(g1,g2)
    c: Coincident(g2,g3)
    c: Coincident(g3,g0)
    c: Vertical(g0)
    c: Vertical(g2)
    c: Horizontal(g1)
    c: Horizontal(g3)
    c: Coincident(g0,g-3)
    c: Coincident(g1,g-4)
FEATURE [PartDesign::Pad] Pad009
  Direction = (0,-1,2e-16)
  Length = 40
  Length2 = 10
  Placement = pos=(0,0,0) rot=(1,0,0;1.5708rad)
  Profile = -> Sketch014
  ReferenceAxis = -> Sketch014 [N_Axis]
  Refine = true
  Suppressed = false
  Type = 0
FEATURE [Sketcher::SketchObject] Sketch015
  ArcFitTolerance = 1e-06
  AttachmentSupport = -> [Pad009]
  ExternalGeometry = -> [Pad009]
  FullyConstrained = true
  MakeInternals = false
  MapMode = 5
  Placement = pos=(0,-5.49e-14,-498.872) rot=(0,0,1;3.14159rad)
  sketch-geometry (4):
    g0: LineSegment StartX=536.684 StartY=850 StartZ=0 EndX=536.684 EndY=826 EndZ=0
    g1: LineSegment StartX=536.684 StartY=826 StartZ=0 EndX=658.316 EndY=826 EndZ=0
    g2: LineSegment StartX=658.316 StartY=826 StartZ=0 EndX=658.316 EndY=850 EndZ=0
    g3: LineSegment StartX=658.316 StartY=850 StartZ=0 EndX=536.684 EndY=850 EndZ=0
  constraints (12):
    c: Coincident(g0,g1)
    c: Coincident(g1,g2)
    c: Coincident(g2,g3)
    c: Coincident(g3,g0)
    c: Vertical(g0)
    c: Vertical(g2)
    c: Horizontal(g1)
    c: Horizontal(g3)
    c: DistanceX(g1,g-4) = 15
    c: DistanceY(g-4,g1) = 1
    c: DistanceY(g0,g-3) = 15
    c: DistanceX(g-3,g0) = 15
FEATURE [PartDesign::Pocket] Pocket005
  BaseFeature = -> Pad009
  Direction = (0,0,-1)
  Length = 5
  Length2 = 5
  Placement = pos=(0,0,0) rot=(1,0,0;1.5708rad)
  Profile = -> Sketch015
  ReferenceAxis = -> Sketch015 [N_Axis]
  Refine = true
  Suppressed = false
  Type = 1
FEATURE [PartDesign::Fillet] Fillet006
  Base = -> Pocket005 [Edge22,Edge21,Edge4,Edge20]
  BaseFeature = -> Pocket005
  Placement = pos=(0,0,0) rot=(1,0,0;1.5708rad)
  Radius = 15
  Refine = true
  SupportTransform = false
  Suppressed = false
  UseAllEdges = false
FEATURE [PartDesign::Fillet] Fillet007
  Base = -> Fillet006 [Edge10,Edge1,Edge20,Edge4]
  BaseFeature = -> Fillet006
  Placement = pos=(0,0,0) rot=(1,0,0;1.5708rad)
  Radius = 5
  Refine = true
  SupportTransform = false
  Suppressed = false
  UseAllEdges = false
FEATURE [PartDesign::Body] Body004
  AllowCompound = false
  Group = -> [DatumPlane003,CopyPocket004,Sketch014,Pad009,Sketch015,Pocket005,Fillet006,Fillet007]
  Origin = -> Origin009
  Tip = -> Fillet007
FEATURE [PartDesign::ShapeBinder] CopyPocket005
  Placement = pos=(0,0,0) rot=(1,0,0;1.5708rad)
  TraceSupport = false
FEATURE [PartDesign::Plane] DatumPlane004
  AttachmentSupport = -> [CopyPocket005]
  Length = 840.637
  MapMode = 5
  Placement = pos=(0,-825,6.6e-15) rot=(1,0,0;1.5708rad)
  ResizeMode = 0
  Width = 867.464
FEATURE [Sketcher::SketchObject] Sketch016
  ArcFitTolerance = 1e-06
  AttachmentSupport = -> [CopyPocket005]
  ExternalGeometry = -> [CopyPocket005]
  FullyConstrained = true
  MakeInternals = false
  MapMode = 5
  Placement = pos=(0,-825,1.897e-13) rot=(1,0,0;1.5708rad)
  sketch-geometry (4):
    g0: LineSegment StartX=-673.316 StartY=-678.872 StartZ=0 EndX=-673.316 EndY=-700.143 EndZ=0
    g1: LineSegment StartX=-673.316 StartY=-700.143 StartZ=0 EndX=-521.684 EndY=-700.143 EndZ=0
    g2: LineSegment StartX=-521.684 StartY=-700.143 StartZ=0 EndX=-521.684 EndY=-678.872 EndZ=0
    g3: LineSegment StartX=-521.684 StartY=-678.872 StartZ=0 EndX=-673.316 EndY=-678.872 EndZ=0
  constraints (10):
    c: Coincident(g0,g1)
    c: Coincident(g1,g2)
    c: Coincident(g2,g3)
    c: Coincident(g3,g0)
    c: Vertical(g0)
    c: Vertical(g2)
    c: Horizontal(g1)
    c: Horizontal(g3)
    c: Coincident(g0,g-4)
    c: Coincident(g1,g-3)
FEATURE [PartDesign::Pad] Pad010
  Direction = (0,-1,2e-16)
  Length = 40
  Length2 = 10
  Placement = pos=(0,0,0) rot=(1,0,0;1.5708rad)
  Profile = -> Sketch016
  ReferenceAxis = -> Sketch016 [N_Axis]
  Refine = true
  Suppressed = false
  Type = 0
FEATURE [Sketcher::SketchObject] Sketch017
  ArcFitTolerance = 1e-06
  AttachmentSupport = -> [Pad010]
  ExternalGeometry = -> [Pad010]
  FullyConstrained = true
  MakeInternals = false
  MapMode = 5
  Placement = pos=(0,-7.47e-14,-678.872) rot=(0,0,1;3.14159rad)
  sketch-geometry (4):
    g0: LineSegment StartX=536.684 StartY=850 StartZ=0 EndX=536.684 EndY=826 EndZ=0
    g1: LineSegment StartX=536.684 StartY=826 StartZ=0 EndX=658.316 EndY=826 EndZ=0
    g2: LineSegment StartX=658.316 StartY=826 StartZ=0 EndX=658.316 EndY=850 EndZ=0
    g3: LineSegment StartX=658.316 StartY=850 StartZ=0 EndX=536.684 EndY=850 EndZ=0
  constraints (12):
    c: Coincident(g0,g1)
    c: Coincident(g1,g2)
    c: Coincident(g2,g3)
    c: Coincident(g3,g0)
    c: Vertical(g0)
    c: Vertical(g2)
    c: Horizontal(g1)
    c: Horizontal(g3)
    c: DistanceY(g2,g-4) = 15
    c: DistanceX(g1,g-4) = 15
    c: DistanceY(g-4,g1) = 1
    c: DistanceX(g-3,g0) = 15
FEATURE [PartDesign::Pocket] Pocket006
  BaseFeature = -> Pad010
  Direction = (0,0,-1)
  Length = 5
  Length2 = 5
  Placement = pos=(0,0,0) rot=(1,0,0;1.5708rad)
  Profile = -> Sketch017
  ReferenceAxis = -> Sketch017 [N_Axis]
  Refine = true
  Suppressed = false
  Type = 1
FEATURE [PartDesign::Fillet] Fillet008
  Base = -> Pocket006 [Edge4,Edge20,Edge21,Edge22]
  BaseFeature = -> Pocket006
  Placement = pos=(0,0,0) rot=(1,0,0;1.5708rad)
  Radius = 15
  Refine = true
  SupportTransform = false
  Suppressed = false
  UseAllEdges = false
FEATURE [PartDesign::Fillet] Fillet009
  Base = -> Fillet008 [Edge8,Edge10,Edge26,Edge20]
  BaseFeature = -> Fillet008
  Placement = pos=(0,0,0) rot=(1,0,0;1.5708rad)
  Radius = 5
  Refine = true
  SupportTransform = false
  Suppressed = false
  UseAllEdges = false
FEATURE [PartDesign::Body] Body005
  AllowCompound = false
  Group = -> [DatumPlane004,CopyPocket005,Sketch016,Pad010,Sketch017,Pocket006,Fillet008,Fillet009]
  Origin = -> Origin010
  Tip = -> Fillet009
FEATURE [PartDesign::ShapeBinder] CopyPocket006
  Placement = pos=(0,0,0) rot=(1,0,0;1.5708rad)
  TraceSupport = false
FEATURE [PartDesign::Plane] DatumPlane005
  AttachmentSupport = -> [CopyPocket006]
  Length = 857.323
  MapMode = 5
  Placement = pos=(0,-825,6.6e-15) rot=(1,0,0;1.5708rad)
  ResizeMode = 0
  Width = 1064.15
FEATURE [Sketcher::SketchObject] Sketch018
  ArcFitTolerance = 1e-06
  AttachmentSupport = -> [CopyPocket006]
  ExternalGeometry = -> [CopyPocket006]
  FullyConstrained = true
  MakeInternals = false
  MapMode = 5
  Placement = pos=(0,-825,1.897e-13) rot=(1,0,0;1.5708rad)
  sketch-geometry (4):
    g0: LineSegment StartX=-673.316 StartY=-858.872 StartZ=0 EndX=-673.316 EndY=-880.143 EndZ=0
    g1: LineSegment StartX=-673.316 StartY=-880.143 StartZ=0 EndX=-521.684 EndY=-880.143 EndZ=0
    g2: LineSegment StartX=-521.684 StartY=-880.143 StartZ=0 EndX=-521.684 EndY=-858.872 EndZ=0
    g3: LineSegment StartX=-521.684 StartY=-858.872 StartZ=0 EndX=-673.316 EndY=-858.872 EndZ=0
  constraints (10):
    c: Coincident(g0,g1)
    c: Coincident(g1,g2)
    c: Coincident(g2,g3)
    c: Coincident(g3,g0)
    c: Vertical(g0)
    c: Vertical(g2)
    c: Horizontal(g1)
    c: Horizontal(g3)
    c: Coincident(g0,g-3)
    c: Coincident(g1,g-4)
FEATURE [PartDesign::Pad] Pad011
  Direction = (0,-1,2e-16)
  Length = 40
  Length2 = 10
  Placement = pos=(0,0,0) rot=(1,0,0;1.5708rad)
  Profile = -> Sketch018
  ReferenceAxis = -> Sketch018 [N_Axis]
  Refine = true
  Suppressed = false
  Type = 0
FEATURE [Sketcher::SketchObject] Sketch019
  ArcFitTolerance = 1e-06
  AttachmentSupport = -> [Pad011]
  ExternalGeometry = -> [Pad011]
  FullyConstrained = true
  MakeInternals = false
  MapMode = 5
  Placement = pos=(0,-9.45e-14,-858.872) rot=(0,0,1;3.14159rad)
  sketch-geometry (4):
    g0: LineSegment StartX=536.684 StartY=850 StartZ=0 EndX=536.684 EndY=826 EndZ=0
    g1: LineSegment StartX=536.684 StartY=826 StartZ=0 EndX=658.316 EndY=826 EndZ=0
    g2: LineSegment StartX=658.316 StartY=826 StartZ=0 EndX=658.316 EndY=850 EndZ=0
    g3: LineSegment StartX=658.316 StartY=850 StartZ=0 EndX=536.684 EndY=850 EndZ=0
  constraints (12):
    c: Coincident(g0,g1)
    c: Coincident(g1,g2)
    c: Coincident(g2,g3)
    c: Coincident(g3,g0)
    c: Vertical(g0)
    c: Vertical(g2)
    c: Horizontal(g1)
    c: Horizontal(g3)
    c: DistanceX(g1,g-4) = 15
    c: DistanceY(g2,g-4) = 15
    c: DistanceX(g-3,g0) = 15
    c: DistanceY(g-4,g1) = 1
FEATURE [PartDesign::Pocket] Pocket007
  BaseFeature = -> Pad011
  Direction = (0,0,-1)
  Length = 1
  Length2 = 5
  Placement = pos=(0,0,0) rot=(1,0,0;1.5708rad)
  Profile = -> Sketch019
  ReferenceAxis = -> Sketch019 [N_Axis]
  Refine = true
  Suppressed = false
  Type = 1
FEATURE [PartDesign::Fillet] Fillet010
  Base = -> Pocket007 [Edge4,Edge20,Edge22,Edge21]
  BaseFeature = -> Pocket007
  Placement = pos=(0,0,0) rot=(1,0,0;1.5708rad)
  Radius = 15
  Refine = true
  SupportTransform = false
  Suppressed = false
  UseAllEdges = false
FEATURE [PartDesign::Fillet] Fillet011
  Base = -> Fillet010 [Edge10,Edge26,Edge8,Edge20]
  BaseFeature = -> Fillet010
  Placement = pos=(0,0,0) rot=(1,0,0;1.5708rad)
  Radius = 5
  Refine = true
  SupportTransform = false
  Suppressed = false
  UseAllEdges = false
FEATURE [PartDesign::Body] Body006
  AllowCompound = false
  Group = -> [DatumPlane005,CopyPocket006,Sketch018,Pad011,Sketch019,Pocket007,Fillet010,Fillet011]
  Origin = -> Origin011
  Tip = -> Fillet011
FEATURE [PartDesign::ShapeBinder] CopyPocket007
  Placement = pos=(0,0,0) rot=(1,0,0;1.5708rad)
  TraceSupport = false
FEATURE [PartDesign::Plane] DatumPlane006
  AttachmentSupport = -> [CopyPocket007]
  Length = 748.322
  MapMode = 5
  Placement = pos=(0,-825,6.6e-15) rot=(1,0,0;1.5708rad)
  ResizeMode = 0
  Width = 171.593
FEATURE [Sketcher::SketchObject] Sketch020
  ArcFitTolerance = 1e-06
  AttachmentSupport = -> [CopyPocket007]
  ExternalGeometry = -> [CopyPocket007]
  FullyConstrained = true
  MakeInternals = false
  MapMode = 5
  Placement = pos=(0,-825,1.897e-13) rot=(1,0,0;1.5708rad)
  sketch-geometry (4):
    g0: LineSegment StartX=515.24 StartY=-68.8715 StartZ=0 EndX=515.24 EndY=-90.1429 EndZ=0
    g1: LineSegment StartX=515.24 StartY=-90.1429 StartZ=0 EndX=666.872 EndY=-90.1429 EndZ=0
    g2: LineSegment StartX=666.872 StartY=-90.1429 StartZ=0 EndX=666.872 EndY=-68.8715 EndZ=0
    g3: LineSegment StartX=666.872 StartY=-68.8715 StartZ=0 EndX=515.24 EndY=-68.8715 EndZ=0
  constraints (10):
    c: Coincident(g0,g1)
    c: Coincident(g1,g2)
    c: Coincident(g2,g3)
    c: Coincident(g3,g0)
    c: Vertical(g0)
    c: Vertical(g2)
    c: Horizontal(g1)
    c: Horizontal(g3)
    c: Coincident(g0,g-3)
    c: Coincident(g1,g-4)
FEATURE [PartDesign::Pad] Pad012
  Direction = (0,-1,2e-16)
  Length = 40
  Length2 = 10
  Placement = pos=(0,0,0) rot=(1,0,0;1.5708rad)
  Profile = -> Sketch020
  ReferenceAxis = -> Sketch020 [N_Axis]
  Refine = true
  Suppressed = false
  Type = 0
FEATURE [Sketcher::SketchObject] Sketch021
  ArcFitTolerance = 1e-06
  AttachmentSupport = -> [Pad012]
  ExternalGeometry = -> [Pad012]
  FullyConstrained = true
  MakeInternals = false
  MapMode = 5
  Placement = pos=(0,-7.6e-15,-68.8715) rot=(0,0,1;3.14159rad)
  sketch-geometry (4):
    g0: LineSegment StartX=-651.872 StartY=850 StartZ=0 EndX=-651.872 EndY=826 EndZ=0
    g1: LineSegment StartX=-651.872 StartY=826 StartZ=0 EndX=-530.24 EndY=826 EndZ=0
    g2: LineSegment StartX=-530.24 StartY=826 StartZ=0 EndX=-530.24 EndY=850 EndZ=0
    g3: LineSegment StartX=-530.24 StartY=850 StartZ=0 EndX=-651.872 EndY=850 EndZ=0
  constraints (12):
    c: Coincident(g0,g1)
    c: Coincident(g1,g2)
    c: Coincident(g2,g3)
    c: Coincident(g3,g0)
    c: Vertical(g0)
    c: Vertical(g2)
    c: Horizontal(g1)
    c: Horizontal(g3)
    c: DistanceX(g2,g-4) = 15
    c: DistanceX(g-3,g0) = 15
    c: DistanceY(g-3,g0) = 1
    c: DistanceY(g2,g-4) = 15
FEATURE [PartDesign::Pocket] Pocket008
  BaseFeature = -> Pad012
  Direction = (0,0,-1)
  Length = 5
  Length2 = 5
  Placement = pos=(0,0,0) rot=(1,0,0;1.5708rad)
  Profile = -> Sketch021
  ReferenceAxis = -> Sketch021 [N_Axis]
  Refine = true
  Suppressed = false
  Type = 1
FEATURE [PartDesign::Fillet] Fillet012
  Base = -> Pocket008 [Edge4,Edge20,Edge21,Edge22]
  BaseFeature = -> Pocket008
  Placement = pos=(0,0,0) rot=(1,0,0;1.5708rad)
  Radius = 15
  Refine = true
  SupportTransform = false
  Suppressed = false
  UseAllEdges = false
FEATURE [PartDesign::Fillet] Fillet013
  Base = -> Fillet012 [Edge10,Edge26,Edge8,Edge20]
  BaseFeature = -> Fillet012
  Placement = pos=(0,0,0) rot=(1,0,0;1.5708rad)
  Radius = 5
  Refine = true
  SupportTransform = false
  Suppressed = false
  UseAllEdges = false
FEATURE [PartDesign::Body] Body007
  AllowCompound = false
  Group = -> [DatumPlane006,CopyPocket007,Sketch020,Pad012,Sketch021,Pocket008,Fillet012,Fillet013]
  Origin = -> Origin012
  Tip = -> Fillet013
FEATURE [PartDesign::ShapeBinder] CopyPocket008
  Placement = pos=(0,0,0) rot=(1,0,0;1.5708rad)
  TraceSupport = false
FEATURE [PartDesign::Plane] DatumPlane007
  AttachmentSupport = -> [CopyPocket008]
  Length = 791.707
  MapMode = 5
  Placement = pos=(0,-825,6.6e-15) rot=(1,0,0;1.5708rad)
  ResizeMode = 0
  Width = 459.977
FEATURE [Sketcher::SketchObject] Sketch022
  ArcFitTolerance = 1e-06
  AttachmentSupport = -> [CopyPocket008]
  ExternalGeometry = -> [CopyPocket008]
  FullyConstrained = true
  MakeInternals = false
  MapMode = 5
  Placement = pos=(0,-825,1.897e-13) rot=(1,0,0;1.5708rad)
  sketch-geometry (4):
    g0: LineSegment StartX=515.24 StartY=-313.872 StartZ=0 EndX=515.24 EndY=-335.143 EndZ=0
    g1: LineSegment StartX=515.24 StartY=-335.143 StartZ=0 EndX=666.872 EndY=-335.143 EndZ=0
    g2: LineSegment StartX=666.872 StartY=-335.143 StartZ=0 EndX=666.872 EndY=-313.872 EndZ=0
    g3: LineSegment StartX=666.872 StartY=-313.872 StartZ=0 EndX=515.24 EndY=-313.872 EndZ=0
  constraints (10):
    c: Coincident(g0,g1)
    c: Coincident(g1,g2)
    c: Coincident(g2,g3)
    c: Coincident(g3,g0)
    c: Vertical(g0)
    c: Vertical(g2)
    c: Horizontal(g1)
    c: Horizontal(g3)
    c: Coincident(g0,g-3)
    c: Coincident(g1,g-4)
FEATURE [PartDesign::Pad] Pad013
  Direction = (0,-1,2e-16)
  Length = 40
  Length2 = 10
  Placement = pos=(0,0,0) rot=(1,0,0;1.5708rad)
  Profile = -> Sketch022
  ReferenceAxis = -> Sketch022 [N_Axis]
  Refine = true
  Suppressed = false
  Type = 0
FEATURE [Sketcher::SketchObject] Sketch023
  ArcFitTolerance = 1e-06
  AttachmentSupport = -> [Pad013]
  ExternalGeometry = -> [Pad013]
  FullyConstrained = true
  MakeInternals = false
  MapMode = 5
  Placement = pos=(0,-3.45e-14,-313.872) rot=(0,0,1;3.14159rad)
  sketch-geometry (4):
    g0: LineSegment StartX=-651.872 StartY=850 StartZ=0 EndX=-651.872 EndY=826 EndZ=0
    g1: LineSegment StartX=-651.872 StartY=826 StartZ=0 EndX=-530.24 EndY=826 EndZ=0
    g2: LineSegment StartX=-530.24 StartY=826 StartZ=0 EndX=-530.24 EndY=850 EndZ=0
    g3: LineSegment StartX=-530.24 StartY=850 StartZ=0 EndX=-651.872 EndY=850 EndZ=0
  constraints (12):
    c: Coincident(g0,g1)
    c: Coincident(g1,g2)
    c: Coincident(g2,g3)
    c: Coincident(g3,g0)
    c: Vertical(g0)
    c: Vertical(g2)
    c: Horizontal(g1)
    c: Horizontal(g3)
    c: DistanceX(g2,g-4) = 15
    c: DistanceY(g2,g-4) = 15
    c: DistanceY(g-4,g1) = 1
    c: DistanceX(g-3,g0) = 15
FEATURE [PartDesign::Pocket] Pocket009
  BaseFeature = -> Pad013
  Direction = (0,0,-1)
  Length = 5
  Length2 = 5
  Placement = pos=(0,0,0) rot=(1,0,0;1.5708rad)
  Profile = -> Sketch023
  ReferenceAxis = -> Sketch023 [N_Axis]
  Refine = true
  Suppressed = false
  Type = 1
FEATURE [PartDesign::Fillet] Fillet014
  Base = -> Pocket009 [Edge4,Edge20,Edge21,Edge22]
  BaseFeature = -> Pocket009
  Placement = pos=(0,0,0) rot=(1,0,0;1.5708rad)
  Radius = 15
  Refine = true
  SupportTransform = false
  Suppressed = false
  UseAllEdges = false
FEATURE [PartDesign::Fillet] Fillet015
  Base = -> Fillet014 [Edge10,Edge26,Edge8,Edge20]
  BaseFeature = -> Fillet014
  Placement = pos=(0,0,0) rot=(1,0,0;1.5708rad)
  Radius = 5
  Refine = true
  SupportTransform = false
  Suppressed = false
  UseAllEdges = false
FEATURE [PartDesign::Body] Body008
  AllowCompound = false
  Group = -> [DatumPlane007,CopyPocket008,Sketch022,Pad013,Sketch023,Pocket009,Fillet014,Fillet015]
  Origin = -> Origin013
  Tip = -> Fillet015
FEATURE [PartDesign::ShapeBinder] CopyPocket009
  Placement = pos=(0,0,0) rot=(1,0,0;1.5708rad)
  TraceSupport = false
FEATURE [PartDesign::Plane] DatumPlane008
  AttachmentSupport = -> [CopyPocket009]
  Length = 814.7
  MapMode = 5
  Placement = pos=(0,-825,6.6e-15) rot=(1,0,0;1.5708rad)
  ResizeMode = 0
  Width = 667.971
FEATURE [Sketcher::SketchObject] Sketch024
  ArcFitTolerance = 1e-06
  AttachmentSupport = -> [CopyPocket009]
  ExternalGeometry = -> [CopyPocket009]
  FullyConstrained = true
  MakeInternals = false
  MapMode = 5
  Placement = pos=(0,-825,1.897e-13) rot=(1,0,0;1.5708rad)
  sketch-geometry (4):
    g0: LineSegment StartX=515.24 StartY=-498.872 StartZ=0 EndX=515.24 EndY=-520.143 EndZ=0
    g1: LineSegment StartX=515.24 StartY=-520.143 StartZ=0 EndX=666.872 EndY=-520.143 EndZ=0
    g2: LineSegment StartX=666.872 StartY=-520.143 StartZ=0 EndX=666.872 EndY=-498.872 EndZ=0
    g3: LineSegment StartX=666.872 StartY=-498.872 StartZ=0 EndX=515.24 EndY=-498.872 EndZ=0
  constraints (10):
    c: Coincident(g0,g1)
    c: Coincident(g1,g2)
    c: Coincident(g2,g3)
    c: Coincident(g3,g0)
    c: Vertical(g0)
    c: Vertical(g2)
    c: Horizontal(g1)
    c: Horizontal(g3)
    c: Coincident(g0,g-3)
    c: Coincident(g1,g-4)
FEATURE [PartDesign::Pad] Pad014
  Direction = (0,-1,2e-16)
  Length = 40
  Length2 = 10
  Placement = pos=(0,0,0) rot=(1,0,0;1.5708rad)
  Profile = -> Sketch024
  ReferenceAxis = -> Sketch024 [N_Axis]
  Refine = true
  Suppressed = false
  Type = 0
FEATURE [Sketcher::SketchObject] Sketch025
  ArcFitTolerance = 1e-06
  AttachmentSupport = -> [Pad014]
  ExternalGeometry = -> [Pad014]
  FullyConstrained = true
  MakeInternals = false
  MapMode = 5
  Placement = pos=(0,-5.49e-14,-498.872) rot=(0,0,1;3.14159rad)
  sketch-geometry (4):
    g0: LineSegment StartX=-651.872 StartY=850 StartZ=0 EndX=-651.872 EndY=826 EndZ=0
    g1: LineSegment StartX=-651.872 StartY=826 StartZ=0 EndX=-530.24 EndY=826 EndZ=0
    g2: LineSegment StartX=-530.24 StartY=826 StartZ=0 EndX=-530.24 EndY=850 EndZ=0
    g3: LineSegment StartX=-530.24 StartY=850 StartZ=0 EndX=-651.872 EndY=850 EndZ=0
  constraints (12):
    c: Coincident(g0,g1)
    c: Coincident(g1,g2)
    c: Coincident(g2,g3)
    c: Coincident(g3,g0)
    c: Vertical(g0)
    c: Vertical(g2)
    c: Horizontal(g1)
    c: Horizontal(g3)
    c: DistanceX(g2,g-4) = 15
    c: DistanceY(g2,g-4) = 15
    c: DistanceY(g-4,g1) = 1
    c: DistanceX(g-3,g0) = 15
FEATURE [PartDesign::Pocket] Pocket010
  BaseFeature = -> Pad014
  Direction = (0,0,-1)
  Length = 5
  Length2 = 5
  Placement = pos=(0,0,0) rot=(1,0,0;1.5708rad)
  Profile = -> Sketch025
  ReferenceAxis = -> Sketch025 [N_Axis]
  Refine = true
  Suppressed = false
  Type = 1
FEATURE [PartDesign::Fillet] Fillet016
  Base = -> Pocket010 [Edge20,Edge4,Edge22,Edge21]
  BaseFeature = -> Pocket010
  Placement = pos=(0,0,0) rot=(1,0,0;1.5708rad)
  Radius = 15
  Refine = true
  SupportTransform = false
  Suppressed = false
  UseAllEdges = false
FEATURE [PartDesign::Fillet] Fillet017
  Base = -> Fillet016 [Edge10,Edge8,Edge26,Edge20]
  BaseFeature = -> Fillet016
  Placement = pos=(0,0,0) rot=(1,0,0;1.5708rad)
  Radius = 5
  Refine = true
  SupportTransform = false
  Suppressed = false
  UseAllEdges = false
FEATURE [PartDesign::Body] Body009
  AllowCompound = false
  Group = -> [DatumPlane008,CopyPocket009,Sketch024,Pad014,Sketch025,Pocket010,Fillet016,Fillet017]
  Origin = -> Origin014
  Tip = -> Fillet017
FEATURE [PartDesign::ShapeBinder] CopyPocket010
  Placement = pos=(0,0,0) rot=(1,0,0;1.5708rad)
  TraceSupport = false
FEATURE [PartDesign::Plane] DatumPlane009
  AttachmentSupport = -> [CopyPocket010]
  Length = 833.535
  MapMode = 5
  Placement = pos=(0,-825,6.6e-15) rot=(1,0,0;1.5708rad)
  ResizeMode = 0
  Width = 866.806
FEATURE [Sketcher::SketchObject] Sketch026
  ArcFitTolerance = 1e-06
  AttachmentSupport = -> [CopyPocket010]
  ExternalGeometry = -> [CopyPocket010]
  FullyConstrained = true
  MakeInternals = false
  MapMode = 5
  Placement = pos=(0,-825,1.897e-13) rot=(1,0,0;1.5708rad)
  sketch-geometry (4):
    g0: LineSegment StartX=515.24 StartY=-678.872 StartZ=0 EndX=515.24 EndY=-700.143 EndZ=0
    g1: LineSegment StartX=515.24 StartY=-700.143 StartZ=0 EndX=666.872 EndY=-700.143 EndZ=0
    g2: LineSegment StartX=666.872 StartY=-700.143 StartZ=0 EndX=666.872 EndY=-678.872 EndZ=0
    g3: LineSegment StartX=666.872 StartY=-678.872 StartZ=0 EndX=515.24 EndY=-678.872 EndZ=0
  constraints (10):
    c: Coincident(g0,g1)
    c: Coincident(g1,g2)
    c: Coincident(g2,g3)
    c: Coincident(g3,g0)
    c: Vertical(g0)
    c: Vertical(g2)
    c: Horizontal(g1)
    c: Horizontal(g3)
    c: Coincident(g0,g-3)
    c: Coincident(g1,g-4)
FEATURE [PartDesign::Pad] Pad015
  Direction = (0,-1,2e-16)
  Length = 40
  Length2 = 10
  Placement = pos=(0,0,0) rot=(1,0,0;1.5708rad)
  Profile = -> Sketch026
  ReferenceAxis = -> Sketch026 [N_Axis]
  Refine = true
  Suppressed = false
  Type = 0
FEATURE [Sketcher::SketchObject] Sketch027
  ArcFitTolerance = 1e-06
  AttachmentSupport = -> [Pad015]
  ExternalGeometry = -> [Pad015]
  FullyConstrained = true
  MakeInternals = false
  MapMode = 5
  Placement = pos=(0,-7.47e-14,-678.872) rot=(0,0,1;3.14159rad)
  sketch-geometry (4):
    g0: LineSegment StartX=-651.872 StartY=850 StartZ=0 EndX=-651.872 EndY=826 EndZ=0
    g1: LineSegment StartX=-651.872 StartY=826 StartZ=0 EndX=-530.24 EndY=826 EndZ=0
    g2: LineSegment StartX=-530.24 StartY=826 StartZ=0 EndX=-530.24 EndY=850 EndZ=0
    g3: LineSegment StartX=-530.24 StartY=850 StartZ=0 EndX=-651.872 EndY=850 EndZ=0
  constraints (12):
    c: Coincident(g0,g1)
    c: Coincident(g1,g2)
    c: Coincident(g2,g3)
    c: Coincident(g3,g0)
    c: Vertical(g0)
    c: Vertical(g2)
    c: Horizontal(g1)
    c: Horizontal(g3)
    c: DistanceX(g-3,g0) = 15
    c: DistanceY(g2,g-4) = 15
    c: DistanceX(g2,g-4) = 15
    c: DistanceY(g-4,g1) = 1
FEATURE [PartDesign::Pocket] Pocket011
  BaseFeature = -> Pad015
  Direction = (0,0,-1)
  Length = 5
  Length2 = 5
  Placement = pos=(0,0,0) rot=(1,0,0;1.5708rad)
  Profile = -> Sketch027
  ReferenceAxis = -> Sketch027 [N_Axis]
  Refine = true
  Suppressed = false
  Type = 1
FEATURE [PartDesign::Fillet] Fillet018
  Base = -> Pocket011 [Edge4,Edge20,Edge21,Edge22]
  BaseFeature = -> Pocket011
  Placement = pos=(0,0,0) rot=(1,0,0;1.5708rad)
  Radius = 15
  Refine = true
  SupportTransform = false
  Suppressed = false
  UseAllEdges = false
FEATURE [PartDesign::Fillet] Fillet019
  Base = -> Fillet018 [Edge10,Edge26,Edge8,Edge20]
  BaseFeature = -> Fillet018
  Placement = pos=(0,0,0) rot=(1,0,0;1.5708rad)
  Radius = 5
  Refine = true
  SupportTransform = false
  Suppressed = false
  UseAllEdges = false
FEATURE [PartDesign::Body] Body010
  AllowCompound = false
  Group = -> [DatumPlane009,CopyPocket010,Sketch026,Pad015,Sketch027,Pocket011,Fillet018,Fillet019]
  Origin = -> Origin015
  Tip = -> Fillet019
FEATURE [PartDesign::ShapeBinder] CopyPocket011
  Placement = pos=(0,0,0) rot=(1,0,0;1.5708rad)
  TraceSupport = false
FEATURE [PartDesign::Plane] DatumPlane010
  AttachmentSupport = -> [CopyPocket011]
  Length = 850.143
  MapMode = 5
  Placement = pos=(0,-825,6.6e-15) rot=(1,0,0;1.5708rad)
  ResizeMode = 0
  Width = 1063.41
FEATURE [Sketcher::SketchObject] Sketch028
  ArcFitTolerance = 1e-06
  AttachmentSupport = -> [CopyPocket011]
  ExternalGeometry = -> [CopyPocket011]
  FullyConstrained = true
  MakeInternals = false
  MapMode = 5
  Placement = pos=(0,-825,1.897e-13) rot=(1,0,0;1.5708rad)
  sketch-geometry (4):
    g0: LineSegment StartX=515.24 StartY=-858.872 StartZ=0 EndX=515.24 EndY=-880.143 EndZ=0
    g1: LineSegment StartX=515.24 StartY=-880.143 StartZ=0 EndX=666.872 EndY=-880.143 EndZ=0
    g2: LineSegment StartX=666.872 StartY=-880.143 StartZ=0 EndX=666.872 EndY=-858.872 EndZ=0
    g3: LineSegment StartX=666.872 StartY=-858.872 StartZ=0 EndX=515.24 EndY=-858.872 EndZ=0
  constraints (10):
    c: Coincident(g0,g1)
    c: Coincident(g1,g2)
    c: Coincident(g2,g3)
    c: Coincident(g3,g0)
    c: Vertical(g0)
    c: Vertical(g2)
    c: Horizontal(g1)
    c: Horizontal(g3)
    c: Coincident(g0,g-3)
    c: Coincident(g1,g-4)
FEATURE [PartDesign::Pad] Pad016
  Direction = (0,-1,2e-16)
  Length = 40
  Length2 = 10
  Placement = pos=(0,0,0) rot=(1,0,0;1.5708rad)
  Profile = -> Sketch028
  ReferenceAxis = -> Sketch028 [N_Axis]
  Refine = true
  Suppressed = false
  Type = 0
FEATURE [Sketcher::SketchObject] Sketch029
  ArcFitTolerance = 1e-06
  AttachmentSupport = -> [Pad016]
  ExternalGeometry = -> [Pad016]
  FullyConstrained = true
  MakeInternals = false
  MapMode = 5
  Placement = pos=(0,-9.45e-14,-858.872) rot=(0,0,1;3.14159rad)
  sketch-geometry (4):
    g0: LineSegment StartX=-651.872 StartY=850 StartZ=0 EndX=-651.872 EndY=826 EndZ=0
    g1: LineSegment StartX=-651.872 StartY=826 StartZ=0 EndX=-530.24 EndY=826 EndZ=0
    g2: LineSegment StartX=-530.24 StartY=826 StartZ=0 EndX=-530.24 EndY=850 EndZ=0
    g3: LineSegment StartX=-530.24 StartY=850 StartZ=0 EndX=-651.872 EndY=850 EndZ=0
  constraints (12):
    c: Coincident(g0,g1)
    c: Coincident(g1,g2)
    c: Coincident(g2,g3)
    c: Coincident(g3,g0)
    c: Vertical(g0)
    c: Vertical(g2)
    c: Horizontal(g1)
    c: Horizontal(g3)
    c: DistanceY(g-4,g1) = 1
    c: DistanceX(g2,g-4) = 15
    c: DistanceY(g2,g-4) = 15
    c: DistanceX(g-3,g0) = 15
FEATURE [PartDesign::Pocket] Pocket012
  BaseFeature = -> Pad016
  Direction = (0,0,-1)
  Length = 5
  Length2 = 5
  Placement = pos=(0,0,0) rot=(1,0,0;1.5708rad)
  Profile = -> Sketch029
  ReferenceAxis = -> Sketch029 [N_Axis]
  Refine = true
  Suppressed = false
  Type = 1
FEATURE [PartDesign::Fillet] Fillet020
  Base = -> Pocket012 [Edge4,Edge20,Edge22,Edge21]
  BaseFeature = -> Pocket012
  Placement = pos=(0,0,0) rot=(1,0,0;1.5708rad)
  Radius = 15
  Refine = true
  SupportTransform = false
  Suppressed = false
  UseAllEdges = false
FEATURE [PartDesign::Fillet] Fillet021
  Base = -> Fillet020 [Edge8,Edge10,Edge26,Edge20]
  BaseFeature = -> Fillet020
  Placement = pos=(0,0,0) rot=(1,0,0;1.5708rad)
  Radius = 5
  Refine = true
  SupportTransform = false
  Suppressed = false
  UseAllEdges = false
FEATURE [PartDesign::Body] Body011
  AllowCompound = false
  Group = -> [DatumPlane010,CopyPocket011,Sketch028,Pad016,Sketch029,Pocket012,Fillet020,Fillet021]
  Origin = -> Origin016
  Tip = -> Fillet021
FEATURE [App::Part] Part001  label="handle_p"
  Group = -> [Body001,Body002,Body003,Body004,Body005,Body006,Body007,Body008,Body009,Body010,Body011]
  Origin = -> Origin006
  Placement = pos=(0,412.5,0) rot=(0,0,1;0rad)
FEATURE [Assembly::JointGroup] Joints001
FEATURE [App::Link] handle_p  label="handle_p001"
  LinkPlacement = pos=(0,412.5,1000) rot=(0,0,1;0rad)
  LinkedObject = -> Part001
  Placement = pos=(0,412.5,1000) rot=(0,0,1;0rad)
FEATURE [Assembly::AssemblyObject] Assembly001  label="handle_a"
  Group = -> [Joints001,handle_p]
  Origin = -> Origin018
  Placement = pos=(0,412.5,1000) rot=(0,0,1;0rad)
  Type = Assembly
FEATURE [Part::FeaturePython] Clone  label="body_clone"  # Draft clone (typed FeaturePython)
  AttacherType = Attacher::AttachEngine3D
  Fuse = false
  Objects = -> [Assembly]
  Scale = (1,1,1)
FEATURE [Part::FeaturePython] Clone001  label="handle_clone"  # Draft clone (typed FeaturePython)
  AttacherType = Attacher::AttachEngine3D
  Fuse = false
  Objects = -> [Assembly001]
  Scale = (1,1,1)
FEATURE [PartDesign::ShapeBinder] CopyPad005
  Placement = pos=(0,-20,9e-15) rot=(0,0,1;0rad)
  TraceSupport = false
FEATURE [PartDesign::Plane] DatumPlane011
  AttachmentSupport = -> [CopyPad005]
  Length = 899.662
  MapMode = 5
  Placement = pos=(0,-95,2.55e-14) rot=(1,0,0;1.5708rad)
  ResizeMode = 0
  Width = 1568.05
FEATURE [Sketcher::SketchObject] Sketch030
  ArcFitTolerance = 1e-06
  AttachmentSupport = -> [CopyPad005]
  ExternalGeometry = -> [CopyPad005]
  FullyConstrained = false
  MakeInternals = false
  MapMode = 5
  Placement = pos=(0,-95,2.55e-14) rot=(1,0,0;1.5708rad)
  sketch-geometry (4):
    g0: LineSegment StartX=-351.618 StartY=995.137 StartZ=0 EndX=-351.618 EndY=0 EndZ=0
    g1: LineSegment StartX=-351.618 StartY=0 StartZ=0 EndX=351.618 EndY=0 EndZ=0
    g2: LineSegment StartX=351.618 StartY=0 StartZ=0 EndX=351.618 EndY=995.137 EndZ=0
    g3: ArcOfCircle CenterX=1.05374e-11 CenterY=995.137 CenterZ=0 NormalX=0 NormalY=0 NormalZ=1 AngleXU=0 Radius=351.618 StartAngle=8.98854e-10 EndAngle=3.14159
  constraints (10):
    c: Coincident(g0,g1)
    c: Coincident(g1,g2)
    c: Vertical(g0)
    c: Vertical(g2)
    c: Horizontal(g1)
    c: Coincident(g0,g-4)
    c: Coincident(g1,g-3)
    c: Coincident(g3,g0)
    c: Coincident(g3,g2)
    c: Tangent(g3,g-5)
FEATURE [PartDesign::Pad] Pad017
  Direction = (0,-1,2e-16)
  Length = 5
  Length2 = 10
  Placement = pos=(0,-20,9e-15) rot=(0,0,1;0rad)
  Profile = -> Sketch030
  ReferenceAxis = -> Sketch030 [N_Axis]
  Refine = true
  Suppressed = false
  Type = 0
FEATURE [PartDesign::Body] Body012
  AllowCompound = false
  Group = -> [DatumPlane011,CopyPad005,Sketch030,Pad017]
  Origin = -> Origin020
  Placement = pos=(0,412.5,0) rot=(0,0,1;0rad)
  Tip = -> Pad017
FEATURE [Assembly::JointGroup] Joints002
FEATURE [App::Link] Body013
  LinkPlacement = pos=(0,412.5,1000) rot=(0,0,1;0rad)
  LinkedObject = -> Body012
  Placement = pos=(0,412.5,1000) rot=(0,0,1;0rad)
FEATURE [Assembly::AssemblyObject] Assembly002  label="glass_a"
  Group = -> [Joints002,Body013]
  Origin = -> Origin021
  Placement = pos=(0,412.5,1000) rot=(0,0,1;0rad)
  Type = Assembly
FEATURE [Part::FeaturePython] Clone002  label="glass_clone"  # Draft clone (typed FeaturePython)
  AttacherType = Attacher::AttachEngine3D
  Fuse = false
  Objects = -> [Assembly002]
  Scale = (1,1,1)
FEATURE [App::Part] Part  label="dressing_table"
  Group = -> [Clone,Clone001,Clone002]
  Origin = -> Origin019
